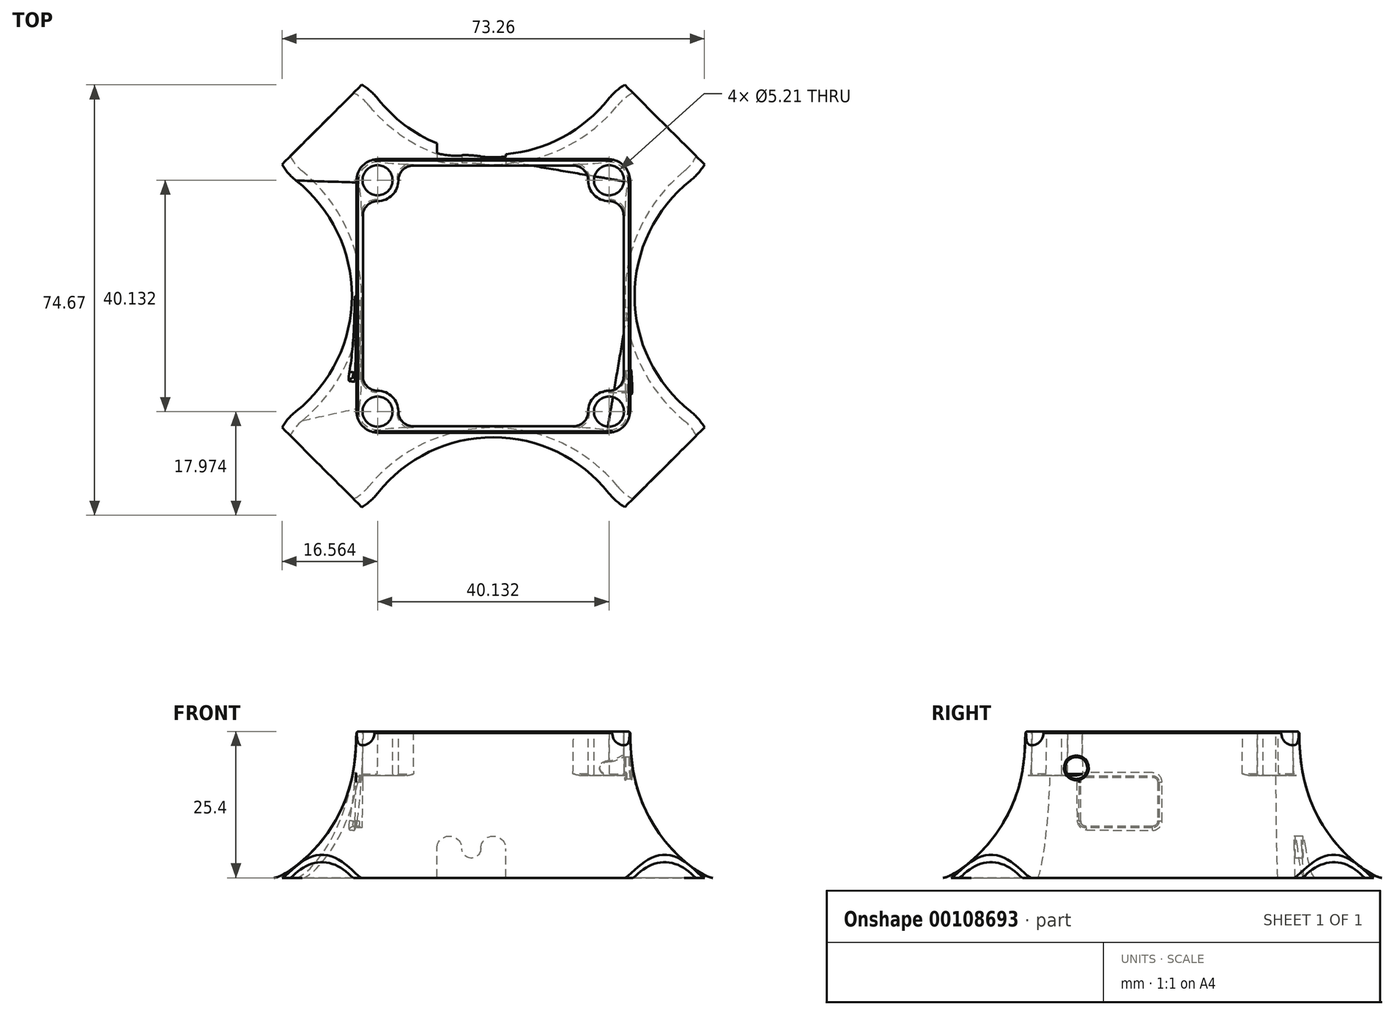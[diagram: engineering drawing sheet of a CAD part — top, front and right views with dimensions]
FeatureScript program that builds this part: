
annotation { "Feature Type Name" : "Feature", "Feature Type Description" : "" }
export const myFeature = defineFeature(function(context is Context, id is Id, definition is map)
    precondition{}
    {
        {
            var Q0;
            Q0=qCreatedBy(makeId("Top.planeOp"),FACE);
            var sketch = newSketch(context, id + "F0", { "sketchPlane" : qUnion([Q0])});
            skPoint(sketch, "E0.middle", {"position": v(0, 0) * mm});
            skCircle(sketch, "E1", {"center": v(-50.04, 0) * mm, "radius": 25.53 * mm});
            skCircle(sketch, "E2", {"center": v(50.04, 0) * mm, "radius": 25.53 * mm});
            skCircle(sketch, "E3", {"center": v(0, 50.04) * mm, "radius": 25.53 * mm});
            skCircle(sketch, "E4", {"center": v(0, -50.04) * mm, "radius": 25.53 * mm});
            skArc(sketch, "E5", {"start": v(-20.02, 34.2) * mm, "mid": v(-35.08, 35.08) * mm, "end": v(-34.2, 20.02) * mm});
            skArc(sketch, "E6", {"start": v(34.2, 20.02) * mm, "mid": v(35.08, 35.08) * mm, "end": v(20.02, 34.2) * mm});
            skArc(sketch, "E7", {"start": v(20.02, -34.2) * mm, "mid": v(35.08, -35.08) * mm, "end": v(34.2, -20.02) * mm});
            skArc(sketch, "E8", {"start": v(-34.2, -20.02) * mm, "mid": v(-35.08, -35.08) * mm, "end": v(-20.02, -34.2) * mm});
            skSolve(sketch);
        }
        {
            var Q0;
            Q0=qCreatedBy(makeId("Top.planeOp"),FACE);
            cPlane(context, id + "F1", {"entities" : qUnion([Q0]), "cplaneType" : CPlaneType.OFFSET, "offset" : 25.4 * mm, "width" : 152.4 * mm, "height" : 152.4 * mm});
        }
        {
            var Q0;
            Q0=qCreatedBy(id+"F1.planeOp",FACE);
            var sketch = newSketch(context, id + "F2", { "sketchPlane" : qUnion([Q0])});
            skLineSegment(sketch, "E9.bottom", {"start": v(19.69, 23.75) * mm, "end": v(-19.69, 23.75) * mm});
            skLineSegment(sketch, "E9.top", {"start": v(19.69, -23.75) * mm, "end": v(-19.69, -23.75) * mm});
            skLineSegment(sketch, "E9.left", {"start": v(23.75, 19.69) * mm, "end": v(23.75, -19.68) * mm});
            skLineSegment(sketch, "E9.right", {"start": v(-23.75, 19.69) * mm, "end": v(-23.75, -19.68) * mm});
            skPoint(sketch, "E9.middle", {"position": v(0, 0) * mm});
            skPoint(sketch, "E10.visualSharp", {"position": v(-23.75, 23.75) * mm});
            skArc(sketch, "E10.filletArc", {"start": v(-19.69, 23.75) * mm, "mid": v(-22.56, 22.56) * mm, "end": v(-23.75, 19.69) * mm});
            skPoint(sketch, "E11.visualSharp", {"position": v(23.75, 23.75) * mm});
            skArc(sketch, "E11.filletArc", {"start": v(23.75, 19.69) * mm, "mid": v(22.56, 22.56) * mm, "end": v(19.69, 23.75) * mm});
            skPoint(sketch, "E12.visualSharp", {"position": v(23.75, -23.75) * mm});
            skArc(sketch, "E12.filletArc", {"start": v(19.69, -23.75) * mm, "mid": v(22.56, -22.56) * mm, "end": v(23.75, -19.68) * mm});
            skPoint(sketch, "E13.visualSharp", {"position": v(-23.75, -23.75) * mm});
            skArc(sketch, "E13.filletArc", {"start": v(-23.75, -19.68) * mm, "mid": v(-22.56, -22.56) * mm, "end": v(-19.69, -23.75) * mm});
            skSolve(sketch);
        }
        {
            var Q0;
            {var subQ4=sQuery(id+"F0.wireOp",EDGE,"mulph02u-d4P1-MrBc-r413-ZnHLI4KnVT8I");var subQ12=sQuery(id+"F0.wireOp",EDGE,"E1");var subQ13=makeQuery(id+"F0.imprint","INTERSECT",VERTEX,{"disambiguationData":[OD(0.0)],"derivedFrom":[subQ12,subQ4]});Q0=makeQuery(id+"F0.imprint","IMPRINT",FACE,{"disambiguationData":[TD([[makeQuery(id+"F0.imprint","IMPRINT",EDGE,{"disambiguationData":[TD([[subQ13,-1.0]])],"derivedFrom":subQ12}),-1.0]])]});}
            var Q1;
            Q1=makeQuery(id+"F2.imprint","IMPRINT",FACE,{"disambiguationData":[TD([[makeQuery(id+"F2.imprint","IMPRINT",EDGE,{"derivedFrom":sQuery(id+"F2.wireOp",EDGE,"E9.bottom")}),1.0]])]});
            loft(context, id + "F3", {"startCondition" : LoftEndDerivativeType.TANGENT_TO_PROFILE, "startMagnitude" : .5, "endCondition" : LoftEndDerivativeType.NORMAL_TO_PROFILE, "endMagnitude" : 2, "sheetProfilesArray" : [{ "sheetProfileEntities" : qUnion([Q0]) }, { "sheetProfileEntities" : qUnion([Q1]) }]});
        }
        {
            var Q0;
            Q0=makeQuery(id+"F3.opLoft","CAP_FACE",FACE,{"disambiguationData":[OSD([makeQuery(id+"F2.imprint","IMPRINT",FACE,{"disambiguationData":[TD([[makeQuery(id+"F2.imprint","IMPRINT",EDGE,{"derivedFrom":sQuery(id+"F2.wireOp",EDGE,"E9.bottom")}),1.0]])]})])],"isStart":true});
            var sketch = newSketch(context, id + "F4", { "sketchPlane" : qUnion([Q0])});
            skLineSegment(sketch, "E14.bottom", {"start": v(19.3, 22.6) * mm, "end": v(-19.3, 22.6) * mm});
            skLineSegment(sketch, "E14.top", {"start": v(19.3, -22.6) * mm, "end": v(-19.3, -22.6) * mm});
            skLineSegment(sketch, "E14.left", {"start": v(22.6, 19.3) * mm, "end": v(22.6, -19.3) * mm});
            skLineSegment(sketch, "E14.right", {"start": v(-22.6, 19.3) * mm, "end": v(-22.6, -19.3) * mm});
            skPoint(sketch, "E14.middle", {"position": v(0, 0) * mm});
            skPoint(sketch, "E15.visualSharp", {"position": v(-22.6, 22.6) * mm});
            skArc(sketch, "E15.filletArc", {"start": v(-19.3, 22.6) * mm, "mid": v(-21.64, 21.64) * mm, "end": v(-22.6, 19.3) * mm});
            skPoint(sketch, "E16.visualSharp", {"position": v(22.6, 22.6) * mm});
            skArc(sketch, "E16.filletArc", {"start": v(22.6, 19.3) * mm, "mid": v(21.64, 21.64) * mm, "end": v(19.3, 22.6) * mm});
            skPoint(sketch, "E17.visualSharp", {"position": v(22.6, -22.6) * mm});
            skArc(sketch, "E17.filletArc", {"start": v(19.3, -22.6) * mm, "mid": v(21.64, -21.64) * mm, "end": v(22.6, -19.3) * mm});
            skPoint(sketch, "E18.visualSharp", {"position": v(-22.6, -22.6) * mm});
            skArc(sketch, "E18.filletArc", {"start": v(-22.6, -19.3) * mm, "mid": v(-21.64, -21.64) * mm, "end": v(-19.3, -22.6) * mm});
            skSolve(sketch);
        }
        {
            var Q0;
            Q0=qCreatedBy(makeId("Top.planeOp"),FACE);
            var sketch = newSketch(context, id + "F5", { "sketchPlane" : qUnion([Q0])});
            skCircle(sketch, "E19", {"center": v(-50.8, 0) * mm, "radius": 27.94 * mm});
            skCircle(sketch, "E20", {"center": v(0, -50.8) * mm, "radius": 27.94 * mm});
            skCircle(sketch, "E21", {"center": v(50.8, 0) * mm, "radius": 27.94 * mm});
            skCircle(sketch, "E22", {"center": v(0, 50.8) * mm, "radius": 27.94 * mm});
            skArc(sketch, "E23", {"start": v(-33.1, -21.62) * mm, "mid": v(-33.71, -33.71) * mm, "end": v(-21.62, -33.1) * mm});
            skArc(sketch, "E24", {"start": v(-21.62, 33.1) * mm, "mid": v(-33.71, 33.71) * mm, "end": v(-33.1, 21.62) * mm});
            skArc(sketch, "E25", {"start": v(33.1, 21.62) * mm, "mid": v(33.71, 33.71) * mm, "end": v(21.62, 33.1) * mm});
            skArc(sketch, "E26", {"start": v(21.62, -33.1) * mm, "mid": v(33.71, -33.71) * mm, "end": v(33.1, -21.62) * mm});
            skSolve(sketch);
        }
        {
            var Q1;
            {var subQ5=sQuery(id+"F5.wireOp",EDGE,"E23");Q1=makeQuery(id+"F5.imprint","IMPRINT",FACE,{"disambiguationData":[TD([[makeQuery(id+"F5.imprint","IMPRINT",EDGE,{"derivedFrom":subQ5}),1.0]])]});}
            var Q2;
            Q2=makeQuery(id+"F4.imprint","IMPRINT",FACE,{"disambiguationData":[TD([[makeQuery(id+"F4.imprint","IMPRINT",EDGE,{"derivedFrom":sQuery(id+"F4.wireOp",EDGE,"E14.bottom")}),1.0]])]});
            loft(context, id + "F6", {"operationType" : NewBodyOperationType.REMOVE, "startCondition" : LoftEndDerivativeType.TANGENT_TO_PROFILE, "startMagnitude" : .5, "endCondition" : LoftEndDerivativeType.NORMAL_TO_PROFILE, "endMagnitude" : 2, "sheetProfilesArray" : [{ "sheetProfileEntities" : qUnion([Q1]) }, { "sheetProfileEntities" : qUnion([Q2]) }]});
        }
        {
            var Q0;
            Q0=qCreatedBy(makeId("Front.planeOp"),FACE);
            var sketch = newSketch(context, id + "F7", { "sketchPlane" : qUnion([Q0])});
            skCircle(sketch, "E27", {"center": v(-7.62, 5.08) * mm, "radius": 2.16 * mm});
            skCircle(sketch, "E28", {"center": v(0, 5.08) * mm, "radius": 2.16 * mm});
            skLineSegment(sketch, "E29.bottom", {"start": v(2.16, 5.08) * mm, "end": v(-2.16, 5.08) * mm});
            skLineSegment(sketch, "E29.top", {"start": v(2.16, 0) * mm, "end": v(-2.16, 0) * mm});
            skLineSegment(sketch, "E29.left", {"start": v(2.16, 5.08) * mm, "end": v(2.16, 0) * mm});
            skLineSegment(sketch, "E29.right", {"start": v(-2.16, 5.08) * mm, "end": v(-2.16, 0) * mm});
            skLineSegment(sketch, "E30.bottom", {"start": v(-5.46, 5.08) * mm, "end": v(-9.78, 5.08) * mm});
            skLineSegment(sketch, "E30.top", {"start": v(-5.46, 0) * mm, "end": v(-9.78, 0) * mm});
            skLineSegment(sketch, "E30.left", {"start": v(-5.46, 5.08) * mm, "end": v(-5.46, 0) * mm});
            skLineSegment(sketch, "E30.right", {"start": v(-9.78, 5.08) * mm, "end": v(-9.78, 0) * mm});
            skArc(sketch, "E31", {"start": v(-5.46, 5.08) * mm, "mid": v(-3.81, 3.43) * mm, "end": v(-2.16, 5.08) * mm});
            skLineSegment(sketch, "E32", {"start": v(-5.46, 0) * mm, "end": v(-2.16, 0) * mm});
            skSolve(sketch);
        }
        {
            var Q0;
            Q0 = qSketchRegion(id + "F7", true);
            extrude(context, id + "F8", {"entities" : qUnion([Q0]), "operationType" : NewBodyOperationType.REMOVE, "endBound" : BoundingType.THROUGH_ALL, "oppositeDirection" : true, "depth" : 25.4 * mm});
        }
        {
            var Q0;
            Q0=qCreatedBy(makeId("Right.planeOp"),FACE);
            var sketch = newSketch(context, id + "F9", { "sketchPlane" : qUnion([Q0])});
            skLineSegment(sketch, "E33.bottom", {"start": v(-14.16, 17.46) * mm, "end": v(-0.83, 17.46) * mm});
            skLineSegment(sketch, "E33.top", {"start": v(-14.16, 8.95) * mm, "end": v(-0.83, 8.95) * mm});
            skLineSegment(sketch, "E33.left", {"start": v(-14.16, 17.46) * mm, "end": v(-14.16, 8.95) * mm});
            skLineSegment(sketch, "E33.right", {"start": v(-0.83, 17.46) * mm, "end": v(-0.83, 8.95) * mm});
            skPoint(sketch, "E33.middle", {"position": v(-7.5, 13.2) * mm});
            skSolve(sketch);
        }
        {
            var Q0;
            Q0 = qSketchRegion(id + "F9", true);
            extrude(context, id + "F10", {"entities" : qUnion([Q0]), "operationType" : NewBodyOperationType.REMOVE, "oppositeDirection" : true, "depth" : 27.94 * mm});
        }
        {
            var Q0;
            Q0=qCreatedBy(id+"F1.planeOp",FACE);
            var sketch = newSketch(context, id + "F11", { "sketchPlane" : qUnion([Q0])});
            skCircle(sketch, "E34", {"center": v(-20.07, 20.07) * mm, "radius": 2.6 * mm});
            skCircle(sketch, "E35", {"center": v(20.07, 20.07) * mm, "radius": 2.6 * mm});
            skCircle(sketch, "E36", {"center": v(20.07, -20.07) * mm, "radius": 2.6 * mm});
            skCircle(sketch, "E37", {"center": v(-20.07, -20.07) * mm, "radius": 2.6 * mm});
            skCircle(sketch, "E38", {"center": v(-20.07, 20.07) * mm, "radius": 3.62 * mm});
            skCircle(sketch, "E39", {"center": v(20.07, 20.07) * mm, "radius": 3.62 * mm});
            skCircle(sketch, "E40", {"center": v(20.07, -20.07) * mm, "radius": 3.62 * mm});
            skCircle(sketch, "E41", {"center": v(-20.07, -20.07) * mm, "radius": 3.62 * mm});
            skSolve(sketch);
        }
        {
            var Q0;
            Q0 = qSketchRegion(id + "F11", true);
            extrude(context, id + "F12", {"entities" : qUnion([Q0]), "operationType" : NewBodyOperationType.ADD, "oppositeDirection" : true, "depth" : 7.62 * mm});
        }
        {
            var Q0;
            Q0=makeQuery(id+"F11.imprint","IMPRINT",FACE,{"disambiguationData":[TD([[makeQuery(id+"F11.imprint","IMPRINT",EDGE,{"derivedFrom":sQuery(id+"F11.wireOp",EDGE,"E34")}),1.0]])]});
            var Q1;
            Q1=makeQuery(id+"F11.imprint","IMPRINT",FACE,{"disambiguationData":[TD([[makeQuery(id+"F11.imprint","IMPRINT",EDGE,{"derivedFrom":sQuery(id+"F11.wireOp",EDGE,"E35")}),1.0]])]});
            var Q2;
            Q2=makeQuery(id+"F11.imprint","IMPRINT",FACE,{"disambiguationData":[TD([[makeQuery(id+"F11.imprint","IMPRINT",EDGE,{"derivedFrom":sQuery(id+"F11.wireOp",EDGE,"E36")}),1.0]])]});
            var Q3;
            Q3=makeQuery(id+"F11.imprint","IMPRINT",FACE,{"disambiguationData":[TD([[makeQuery(id+"F11.imprint","IMPRINT",EDGE,{"derivedFrom":sQuery(id+"F11.wireOp",EDGE,"E37")}),1.0]])]});
            extrude(context, id + "F13", {"entities" : qUnion([Q0, Q1, Q2, Q3]), "operationType" : NewBodyOperationType.REMOVE, "oppositeDirection" : true, "depth" : 25.4 * mm});
        }
        {
            var Q0;
            Q0=qCreatedBy(makeId("Top.planeOp"),FACE);
            var sketch = newSketch(context, id + "F14", { "sketchPlane" : qUnion([Q0])});
            skLineSegment(sketch, "E42", {"start": v(-40.32, -19.12) * mm, "end": v(-21.86, -37.57) * mm});
            skLineSegment(sketch, "E43", {"start": v(-21.86, -37.57) * mm, "end": v(-34.9, -50.6) * mm});
            skLineSegment(sketch, "E44", {"start": v(-34.9, -50.6) * mm, "end": v(-53.35, -32.15) * mm});
            skLineSegment(sketch, "E45", {"start": v(-53.35, -32.15) * mm, "end": v(-40.32, -19.12) * mm});
            skLineSegment(sketch, "E46", {"start": v(18.93, -40.5) * mm, "end": v(41.3, -18.13) * mm});
            skLineSegment(sketch, "E47", {"start": v(41.3, -18.13) * mm, "end": v(54.22, -31.04) * mm});
            skLineSegment(sketch, "E48", {"start": v(54.22, -31.04) * mm, "end": v(31.85, -53.42) * mm});
            skLineSegment(sketch, "E49", {"start": v(31.85, -53.42) * mm, "end": v(18.93, -40.5) * mm});
            skLineSegment(sketch, "E50", {"start": v(19.12, 40.32) * mm, "end": v(39.94, 19.5) * mm});
            skLineSegment(sketch, "E51", {"start": v(39.94, 19.5) * mm, "end": v(51.75, 31.32) * mm});
            skLineSegment(sketch, "E52", {"start": v(51.75, 31.32) * mm, "end": v(30.93, 52.14) * mm});
            skLineSegment(sketch, "E53", {"start": v(30.93, 52.14) * mm, "end": v(19.12, 40.32) * mm});
            skLineSegment(sketch, "E54", {"start": v(-40.03, 19.4) * mm, "end": v(-18.43, 41.01) * mm});
            skLineSegment(sketch, "E55", {"start": v(-18.43, 41.01) * mm, "end": v(-28.85, 51.44) * mm});
            skLineSegment(sketch, "E56", {"start": v(-28.85, 51.44) * mm, "end": v(-50.46, 29.83) * mm});
            skLineSegment(sketch, "E57", {"start": v(-50.46, 29.83) * mm, "end": v(-40.03, 19.4) * mm});
            skSolve(sketch);
        }
        {
            var Q0;
            Q0 = qSketchRegion(id + "F14", true);
            extrude(context, id + "F15", {"entities" : qUnion([Q0]), "operationType" : NewBodyOperationType.REMOVE, "depth" : 7.62 * mm});
        }
        {
            var Q0;
            Q0=makeQuery(id+"F10.boolean.opBoolean","COPY",EDGE,{"derivedFrom":makeQuery(id+"F10.opExtrude","SWEPT_EDGE",EDGE,{"disambiguationData":[OSD([sQuery(id+"F9.wireOp",EDGE,"E33.bottom"),sQuery(id+"F9.wireOp",EDGE,"E33.right")])]})});
            var Q1;
            Q1=makeQuery(id+"F10.boolean.opBoolean","COPY",EDGE,{"derivedFrom":makeQuery(id+"F10.opExtrude","SWEPT_EDGE",EDGE,{"disambiguationData":[OSD([sQuery(id+"F9.wireOp",EDGE,"E33.bottom"),sQuery(id+"F9.wireOp",EDGE,"E33.left")])]})});
            var Q2;
            Q2=makeQuery(id+"F10.boolean.opBoolean","COPY",EDGE,{"derivedFrom":makeQuery(id+"F10.opExtrude","SWEPT_EDGE",EDGE,{"disambiguationData":[OSD([sQuery(id+"F9.wireOp",EDGE,"E33.top"),sQuery(id+"F9.wireOp",EDGE,"E33.right")])]})});
            var Q3;
            Q3=makeQuery(id+"F10.boolean.opBoolean","COPY",EDGE,{"derivedFrom":makeQuery(id+"F10.opExtrude","SWEPT_EDGE",EDGE,{"disambiguationData":[OSD([sQuery(id+"F9.wireOp",EDGE,"E33.top"),sQuery(id+"F9.wireOp",EDGE,"E33.left")])]})});
            fillet(context, id + "F16", {"entities" : qUnion([Q0, Q1, Q2, Q3]), "radius" : 0.89 * mm, "tangentPropagation" : true, "allowEdgeOverflow" : false});
        }
        {
            var Q0;
            Q0=makeQuery(id+"F10.boolean.opBoolean","INTERSECT",EDGE,{"derivedFrom":[makeQuery(id+"F6.boolean.opBoolean","COPY",FACE,{"derivedFrom":makeQuery(id+"F6.opLoft","SWEPT_FACE",FACE,{"disambiguationData":[OSD([sQuery(id+"F4.wireOp",EDGE,"E14.top"),sQuery(id+"F4.wireOp",EDGE,"E14.right"),sQuery(id+"F4.wireOp",EDGE,"E18.filletArc"),sQuery(id+"F5.wireOp",EDGE,"E19"),sQuery(id+"F5.wireOp",EDGE,"E20"),sQuery(id+"F5.wireOp",EDGE,"E23")])]})}),makeQuery(id+"F10.opExtrude","SWEPT_FACE",FACE,{"disambiguationData":[OSD([sQuery(id+"F9.wireOp",EDGE,"E33.bottom")])]})]});
            var Q1;
            Q1=makeQuery(id+"F10.boolean.opBoolean","INTERSECT",EDGE,{"derivedFrom":[makeQuery(id+"F6.boolean.opBoolean","COPY",FACE,{"derivedFrom":makeQuery(id+"F6.opLoft","SWEPT_FACE",FACE,{"disambiguationData":[OSD([sQuery(id+"F4.wireOp",EDGE,"E14.top"),sQuery(id+"F4.wireOp",EDGE,"E14.right"),sQuery(id+"F4.wireOp",EDGE,"E18.filletArc"),sQuery(id+"F5.wireOp",EDGE,"E19"),sQuery(id+"F5.wireOp",EDGE,"E20"),sQuery(id+"F5.wireOp",EDGE,"E23")])]})}),makeQuery(id+"F10.opExtrude","SWEPT_FACE",FACE,{"disambiguationData":[OSD([sQuery(id+"F9.wireOp",EDGE,"E33.left")])]})]});
            var Q2;
            Q2=makeQuery(id+"F10.boolean.opBoolean","INTERSECT",EDGE,{"derivedFrom":[makeQuery(id+"F6.boolean.opBoolean","COPY",FACE,{"derivedFrom":makeQuery(id+"F6.opLoft","SWEPT_FACE",FACE,{"disambiguationData":[OSD([sQuery(id+"F4.wireOp",EDGE,"E14.top"),sQuery(id+"F4.wireOp",EDGE,"E14.right"),sQuery(id+"F4.wireOp",EDGE,"E18.filletArc"),sQuery(id+"F5.wireOp",EDGE,"E19"),sQuery(id+"F5.wireOp",EDGE,"E20"),sQuery(id+"F5.wireOp",EDGE,"E23")])]})}),makeQuery(id+"F10.opExtrude","SWEPT_FACE",FACE,{"disambiguationData":[OSD([sQuery(id+"F9.wireOp",EDGE,"E33.top")])]})]});
            var Q3;
            Q3=makeQuery(id+"F10.boolean.opBoolean","INTERSECT",EDGE,{"derivedFrom":[makeQuery(id+"F6.boolean.opBoolean","COPY",FACE,{"derivedFrom":makeQuery(id+"F6.opLoft","SWEPT_FACE",FACE,{"disambiguationData":[OSD([sQuery(id+"F4.wireOp",EDGE,"E14.top"),sQuery(id+"F4.wireOp",EDGE,"E14.right"),sQuery(id+"F4.wireOp",EDGE,"E18.filletArc"),sQuery(id+"F5.wireOp",EDGE,"E19"),sQuery(id+"F5.wireOp",EDGE,"E20"),sQuery(id+"F5.wireOp",EDGE,"E23")])]})}),makeQuery(id+"F10.opExtrude","SWEPT_FACE",FACE,{"disambiguationData":[OSD([sQuery(id+"F9.wireOp",EDGE,"E33.right")])]})]});
            fillet(context, id + "F17", {"entities" : qUnion([Q0, Q1, Q2, Q3]), "radius" : 0.25 * mm, "tangentPropagation" : true, "allowEdgeOverflow" : false});
        }
        {
            var Q0;
            Q0=makeQuery(id+"F12.boolean.opBoolean","INTERSECT",EDGE,{"disambiguationData":[OD(2.0)],"derivedFrom":[makeQuery(id+"F6.boolean.opBoolean","COPY",FACE,{"derivedFrom":makeQuery(id+"F6.opLoft","SWEPT_FACE",FACE,{"disambiguationData":[OSD([sQuery(id+"F4.wireOp",EDGE,"E14.top"),sQuery(id+"F4.wireOp",EDGE,"E14.right"),sQuery(id+"F4.wireOp",EDGE,"E18.filletArc"),sQuery(id+"F5.wireOp",EDGE,"E19"),sQuery(id+"F5.wireOp",EDGE,"E20"),sQuery(id+"F5.wireOp",EDGE,"E23")])]})}),makeQuery(id+"F12.opExtrude","SWEPT_FACE",FACE,{"disambiguationData":[OSD([sQuery(id+"F11.wireOp",EDGE,"E41")])]})]});
            var Q1;
            Q1=makeQuery(id+"F12.boolean.opBoolean","INTERSECT",EDGE,{"disambiguationData":[OD(1.0)],"derivedFrom":[makeQuery(id+"F6.boolean.opBoolean","COPY",FACE,{"derivedFrom":makeQuery(id+"F6.opLoft","SWEPT_FACE",FACE,{"disambiguationData":[OSD([sQuery(id+"F4.wireOp",EDGE,"E14.top"),sQuery(id+"F4.wireOp",EDGE,"E14.right"),sQuery(id+"F4.wireOp",EDGE,"E18.filletArc"),sQuery(id+"F5.wireOp",EDGE,"E19"),sQuery(id+"F5.wireOp",EDGE,"E20"),sQuery(id+"F5.wireOp",EDGE,"E23")])]})}),makeQuery(id+"F12.opExtrude","SWEPT_FACE",FACE,{"disambiguationData":[OSD([sQuery(id+"F11.wireOp",EDGE,"E41")])]})]});
            var Q2;
            Q2=makeQuery(id+"F12.boolean.opBoolean","INTERSECT",EDGE,{"disambiguationData":[OD(2.0)],"derivedFrom":[makeQuery(id+"F6.boolean.opBoolean","COPY",FACE,{"derivedFrom":makeQuery(id+"F6.opLoft","SWEPT_FACE",FACE,{"disambiguationData":[OSD([sQuery(id+"F4.wireOp",EDGE,"E14.top"),sQuery(id+"F4.wireOp",EDGE,"E14.right"),sQuery(id+"F4.wireOp",EDGE,"E18.filletArc"),sQuery(id+"F5.wireOp",EDGE,"E19"),sQuery(id+"F5.wireOp",EDGE,"E20"),sQuery(id+"F5.wireOp",EDGE,"E23")])]})}),makeQuery(id+"F12.opExtrude","SWEPT_FACE",FACE,{"disambiguationData":[OSD([sQuery(id+"F11.wireOp",EDGE,"E38")])]})]});
            var Q3;
            Q3=makeQuery(id+"F12.boolean.opBoolean","INTERSECT",EDGE,{"disambiguationData":[OD(1.0)],"derivedFrom":[makeQuery(id+"F6.boolean.opBoolean","COPY",FACE,{"derivedFrom":makeQuery(id+"F6.opLoft","SWEPT_FACE",FACE,{"disambiguationData":[OSD([sQuery(id+"F4.wireOp",EDGE,"E14.top"),sQuery(id+"F4.wireOp",EDGE,"E14.right"),sQuery(id+"F4.wireOp",EDGE,"E18.filletArc"),sQuery(id+"F5.wireOp",EDGE,"E19"),sQuery(id+"F5.wireOp",EDGE,"E20"),sQuery(id+"F5.wireOp",EDGE,"E23")])]})}),makeQuery(id+"F12.opExtrude","SWEPT_FACE",FACE,{"disambiguationData":[OSD([sQuery(id+"F11.wireOp",EDGE,"E38")])]})]});
            var Q4;
            Q4=makeQuery(id+"F12.boolean.opBoolean","INTERSECT",EDGE,{"disambiguationData":[OD(2.0)],"derivedFrom":[makeQuery(id+"F6.boolean.opBoolean","COPY",FACE,{"derivedFrom":makeQuery(id+"F6.opLoft","SWEPT_FACE",FACE,{"disambiguationData":[OSD([sQuery(id+"F4.wireOp",EDGE,"E14.top"),sQuery(id+"F4.wireOp",EDGE,"E14.right"),sQuery(id+"F4.wireOp",EDGE,"E18.filletArc"),sQuery(id+"F5.wireOp",EDGE,"E19"),sQuery(id+"F5.wireOp",EDGE,"E20"),sQuery(id+"F5.wireOp",EDGE,"E23")])]})}),makeQuery(id+"F12.opExtrude","SWEPT_FACE",FACE,{"disambiguationData":[OSD([sQuery(id+"F11.wireOp",EDGE,"E39")])]})]});
            var Q5;
            Q5=makeQuery(id+"F12.boolean.opBoolean","INTERSECT",EDGE,{"disambiguationData":[OD(1.0)],"derivedFrom":[makeQuery(id+"F6.boolean.opBoolean","COPY",FACE,{"derivedFrom":makeQuery(id+"F6.opLoft","SWEPT_FACE",FACE,{"disambiguationData":[OSD([sQuery(id+"F4.wireOp",EDGE,"E14.top"),sQuery(id+"F4.wireOp",EDGE,"E14.right"),sQuery(id+"F4.wireOp",EDGE,"E18.filletArc"),sQuery(id+"F5.wireOp",EDGE,"E19"),sQuery(id+"F5.wireOp",EDGE,"E20"),sQuery(id+"F5.wireOp",EDGE,"E23")])]})}),makeQuery(id+"F12.opExtrude","SWEPT_FACE",FACE,{"disambiguationData":[OSD([sQuery(id+"F11.wireOp",EDGE,"E39")])]})]});
            var Q6;
            Q6=makeQuery(id+"F12.boolean.opBoolean","INTERSECT",EDGE,{"disambiguationData":[OD(1.0)],"derivedFrom":[makeQuery(id+"F6.boolean.opBoolean","COPY",FACE,{"derivedFrom":makeQuery(id+"F6.opLoft","SWEPT_FACE",FACE,{"disambiguationData":[OSD([sQuery(id+"F4.wireOp",EDGE,"E14.top"),sQuery(id+"F4.wireOp",EDGE,"E14.right"),sQuery(id+"F4.wireOp",EDGE,"E18.filletArc"),sQuery(id+"F5.wireOp",EDGE,"E19"),sQuery(id+"F5.wireOp",EDGE,"E20"),sQuery(id+"F5.wireOp",EDGE,"E23")])]})}),makeQuery(id+"F12.opExtrude","SWEPT_FACE",FACE,{"disambiguationData":[OSD([sQuery(id+"F11.wireOp",EDGE,"E40")])]})]});
            var Q7;
            Q7=makeQuery(id+"F12.boolean.opBoolean","INTERSECT",EDGE,{"disambiguationData":[OD(2.0)],"derivedFrom":[makeQuery(id+"F6.boolean.opBoolean","COPY",FACE,{"derivedFrom":makeQuery(id+"F6.opLoft","SWEPT_FACE",FACE,{"disambiguationData":[OSD([sQuery(id+"F4.wireOp",EDGE,"E14.top"),sQuery(id+"F4.wireOp",EDGE,"E14.right"),sQuery(id+"F4.wireOp",EDGE,"E18.filletArc"),sQuery(id+"F5.wireOp",EDGE,"E19"),sQuery(id+"F5.wireOp",EDGE,"E20"),sQuery(id+"F5.wireOp",EDGE,"E23")])]})}),makeQuery(id+"F12.opExtrude","SWEPT_FACE",FACE,{"disambiguationData":[OSD([sQuery(id+"F11.wireOp",EDGE,"E40")])]})]});
            fillet(context, id + "F18", {"entities" : qUnion([Q0, Q1, Q2, Q3, Q4, Q5, Q6, Q7]), "radius" : 2.54 * mm, "tangentPropagation" : true, "allowEdgeOverflow" : false});
        }
        {
            var Q0;
            {var subQ0=sQuery(id+"F11.wireOp",EDGE,"E35");Q0=makeQuery(id+"F13.boolean.opBoolean","MERGE",EDGE,{"derivedFrom":[makeQuery(id+"F12.opExtrude","CAP_EDGE",EDGE,{"disambiguationData":[OSD([subQ0])],"isStart":true}),makeQuery(id+"F13.opExtrude","CAP_EDGE",EDGE,{"disambiguationData":[OSD([subQ0])],"isStart":true})]});}
            var Q1;
            {var subQ0=sQuery(id+"F11.wireOp",EDGE,"E34");Q1=makeQuery(id+"F13.boolean.opBoolean","MERGE",EDGE,{"derivedFrom":[makeQuery(id+"F12.opExtrude","CAP_EDGE",EDGE,{"disambiguationData":[OSD([subQ0])],"isStart":true}),makeQuery(id+"F13.opExtrude","CAP_EDGE",EDGE,{"disambiguationData":[OSD([subQ0])],"isStart":true})]});}
            var Q2;
            {var subQ0=sQuery(id+"F11.wireOp",EDGE,"E36");Q2=makeQuery(id+"F13.boolean.opBoolean","MERGE",EDGE,{"derivedFrom":[makeQuery(id+"F12.opExtrude","CAP_EDGE",EDGE,{"disambiguationData":[OSD([subQ0])],"isStart":true}),makeQuery(id+"F13.opExtrude","CAP_EDGE",EDGE,{"disambiguationData":[OSD([subQ0])],"isStart":true})]});}
            var Q3;
            {var subQ0=sQuery(id+"F11.wireOp",EDGE,"E37");Q3=makeQuery(id+"F13.boolean.opBoolean","MERGE",EDGE,{"derivedFrom":[makeQuery(id+"F12.opExtrude","CAP_EDGE",EDGE,{"disambiguationData":[OSD([subQ0])],"isStart":true}),makeQuery(id+"F13.opExtrude","CAP_EDGE",EDGE,{"disambiguationData":[OSD([subQ0])],"isStart":true})]});}
            var Q4;
            Q4=makeQuery(id+"F12.opExtrude","CAP_EDGE",EDGE,{"disambiguationData":[OSD([sQuery(id+"F11.wireOp",EDGE,"E35")])],"isStart":false});
            var Q5;
            Q5=makeQuery(id+"F12.opExtrude","CAP_EDGE",EDGE,{"disambiguationData":[OSD([sQuery(id+"F11.wireOp",EDGE,"E34")])],"isStart":false});
            var Q6;
            Q6=makeQuery(id+"F12.opExtrude","CAP_EDGE",EDGE,{"disambiguationData":[OSD([sQuery(id+"F11.wireOp",EDGE,"E37")])],"isStart":false});
            var Q7;
            Q7=makeQuery(id+"F12.opExtrude","CAP_EDGE",EDGE,{"disambiguationData":[OSD([sQuery(id+"F11.wireOp",EDGE,"E36")])],"isStart":false});
            var Q8;
            {var subQ0=sQuery(id+"F11.wireOp",EDGE,"E40");Q8=makeQuery(id+"FeLZyzeFWoreKK9_1.opFillet","BLEND_EDGE",EDGE,{"blendedFrom":[makeQuery(id+"F12.boolean.opBoolean","INTERSECT",EDGE,{"disambiguationData":[OD(1.0)],"derivedFrom":[makeQuery(id+"F6.boolean.opBoolean","COPY",FACE,{"derivedFrom":makeQuery(id+"F6.opLoft","SWEPT_FACE",FACE,{"disambiguationData":[OSD([sQuery(id+"F4.wireOp",EDGE,"E14.top"),sQuery(id+"F4.wireOp",EDGE,"E14.right"),sQuery(id+"F4.wireOp",EDGE,"E18.filletArc"),sQuery(id+"F5.wireOp",EDGE,"E19"),sQuery(id+"F5.wireOp",EDGE,"E20"),sQuery(id+"F5.wireOp",EDGE,"E23")])]})}),makeQuery(id+"F12.opExtrude","SWEPT_FACE",FACE,{"disambiguationData":[OSD([subQ0])]})]}),makeQuery(id+"F12.opExtrude","CAP_FACE",FACE,{"disambiguationData":[OSD([sQuery(id+"F11.wireOp",EDGE,"E36"),subQ0])],"isStart":false})],"blendedInto":[makeQuery(id+"F12.opExtrude","CAP_FACE",FACE,{"disambiguationData":[OSD([sQuery(id+"F11.wireOp",EDGE,"E36"),subQ0])],"isStart":false})]});}
            var Q9;
            {var subQ0=sQuery(id+"F11.wireOp",EDGE,"E41");Q9=makeQuery(id+"FeLZyzeFWoreKK9_1.opFillet","BLEND_EDGE",EDGE,{"blendedFrom":[makeQuery(id+"F12.boolean.opBoolean","INTERSECT",EDGE,{"disambiguationData":[OD(0.0)],"derivedFrom":[makeQuery(id+"F6.boolean.opBoolean","COPY",FACE,{"derivedFrom":makeQuery(id+"F6.opLoft","SWEPT_FACE",FACE,{"disambiguationData":[OSD([sQuery(id+"F4.wireOp",EDGE,"E14.top"),sQuery(id+"F4.wireOp",EDGE,"E14.right"),sQuery(id+"F4.wireOp",EDGE,"E18.filletArc"),sQuery(id+"F5.wireOp",EDGE,"E19"),sQuery(id+"F5.wireOp",EDGE,"E20"),sQuery(id+"F5.wireOp",EDGE,"E23")])]})}),makeQuery(id+"F12.opExtrude","SWEPT_FACE",FACE,{"disambiguationData":[OSD([subQ0])]})]}),makeQuery(id+"F12.opExtrude","CAP_FACE",FACE,{"disambiguationData":[OSD([sQuery(id+"F11.wireOp",EDGE,"E37"),subQ0])],"isStart":false})],"blendedInto":[makeQuery(id+"F12.opExtrude","CAP_FACE",FACE,{"disambiguationData":[OSD([sQuery(id+"F11.wireOp",EDGE,"E37"),subQ0])],"isStart":false})]});}
            var Q10;
            {var subQ0=sQuery(id+"F11.wireOp",EDGE,"E38");Q10=makeQuery(id+"FeLZyzeFWoreKK9_1.opFillet","BLEND_EDGE",EDGE,{"blendedFrom":[makeQuery(id+"F12.boolean.opBoolean","INTERSECT",EDGE,{"disambiguationData":[OD(1.0)],"derivedFrom":[makeQuery(id+"F6.boolean.opBoolean","COPY",FACE,{"derivedFrom":makeQuery(id+"F6.opLoft","SWEPT_FACE",FACE,{"disambiguationData":[OSD([sQuery(id+"F4.wireOp",EDGE,"E14.top"),sQuery(id+"F4.wireOp",EDGE,"E14.right"),sQuery(id+"F4.wireOp",EDGE,"E18.filletArc"),sQuery(id+"F5.wireOp",EDGE,"E19"),sQuery(id+"F5.wireOp",EDGE,"E20"),sQuery(id+"F5.wireOp",EDGE,"E23")])]})}),makeQuery(id+"F12.opExtrude","SWEPT_FACE",FACE,{"disambiguationData":[OSD([subQ0])]})]}),makeQuery(id+"F12.opExtrude","CAP_FACE",FACE,{"disambiguationData":[OSD([sQuery(id+"F11.wireOp",EDGE,"E34"),subQ0])],"isStart":false})],"blendedInto":[makeQuery(id+"F12.opExtrude","CAP_FACE",FACE,{"disambiguationData":[OSD([sQuery(id+"F11.wireOp",EDGE,"E34"),subQ0])],"isStart":false})]});}
            var Q11;
            {var subQ0=sQuery(id+"F11.wireOp",EDGE,"E39");Q11=makeQuery(id+"FeLZyzeFWoreKK9_1.opFillet","BLEND_EDGE",EDGE,{"blendedFrom":[makeQuery(id+"F12.boolean.opBoolean","INTERSECT",EDGE,{"disambiguationData":[OD(0.0)],"derivedFrom":[makeQuery(id+"F6.boolean.opBoolean","COPY",FACE,{"derivedFrom":makeQuery(id+"F6.opLoft","SWEPT_FACE",FACE,{"disambiguationData":[OSD([sQuery(id+"F4.wireOp",EDGE,"E14.top"),sQuery(id+"F4.wireOp",EDGE,"E14.right"),sQuery(id+"F4.wireOp",EDGE,"E18.filletArc"),sQuery(id+"F5.wireOp",EDGE,"E19"),sQuery(id+"F5.wireOp",EDGE,"E20"),sQuery(id+"F5.wireOp",EDGE,"E23")])]})}),makeQuery(id+"F12.opExtrude","SWEPT_FACE",FACE,{"disambiguationData":[OSD([subQ0])]})]}),makeQuery(id+"F12.opExtrude","CAP_FACE",FACE,{"disambiguationData":[OSD([sQuery(id+"F11.wireOp",EDGE,"E35"),subQ0])],"isStart":false})],"blendedInto":[makeQuery(id+"F12.opExtrude","CAP_FACE",FACE,{"disambiguationData":[OSD([sQuery(id+"F11.wireOp",EDGE,"E35"),subQ0])],"isStart":false})]});}
            var Q12;
            Q12=makeQuery(id+"F6.boolean.opBoolean","COPY",EDGE,{"derivedFrom":makeQuery(id+"F6.opLoft","MID_CAP_EDGE",EDGE,{"disambiguationData":[OSD([sQuery(id+"F4.wireOp",EDGE,"E14.left"),sQuery(id+"F4.wireOp",EDGE,"E16.filletArc"),sQuery(id+"F4.wireOp",EDGE,"E17.filletArc")])],"capPos":1.0})});
            fillet(context, id + "F19", {"entities" : qUnion([Q0, Q1, Q2, Q3, Q4, Q5, Q6, Q7, Q8, Q9, Q10, Q11, Q12]), "radius" : 0.25 * mm, "tangentPropagation" : true, "allowEdgeOverflow" : false});
        }
        {
            var Q0;
            {var subQ0=sQuery(id+"F11.wireOp",EDGE,"E41");Q0=makeQuery(id+"F18.opFillet","BLEND_EDGE",EDGE,{"blendedFrom":[makeQuery(id+"F12.boolean.opBoolean","INTERSECT",EDGE,{"disambiguationData":[OD(1.0)],"derivedFrom":[makeQuery(id+"F6.boolean.opBoolean","COPY",FACE,{"derivedFrom":makeQuery(id+"F6.opLoft","SWEPT_FACE",FACE,{"disambiguationData":[OSD([sQuery(id+"F4.wireOp",EDGE,"E14.top"),sQuery(id+"F4.wireOp",EDGE,"E14.right"),sQuery(id+"F4.wireOp",EDGE,"E18.filletArc"),sQuery(id+"F5.wireOp",EDGE,"E19"),sQuery(id+"F5.wireOp",EDGE,"E20"),sQuery(id+"F5.wireOp",EDGE,"E23")])]})}),makeQuery(id+"F12.opExtrude","SWEPT_FACE",FACE,{"disambiguationData":[OSD([subQ0])]})]}),makeQuery(id+"F12.opExtrude","CAP_FACE",FACE,{"disambiguationData":[OSD([sQuery(id+"F11.wireOp",EDGE,"E37"),subQ0])],"isStart":false})],"blendedInto":[makeQuery(id+"F12.opExtrude","CAP_FACE",FACE,{"disambiguationData":[OSD([sQuery(id+"F11.wireOp",EDGE,"E37"),subQ0])],"isStart":false})]});}
            var Q1;
            {var subQ0=sQuery(id+"F11.wireOp",EDGE,"E40");Q1=makeQuery(id+"F18.opFillet","BLEND_EDGE",EDGE,{"blendedFrom":[makeQuery(id+"F12.boolean.opBoolean","INTERSECT",EDGE,{"disambiguationData":[OD(1.0)],"derivedFrom":[makeQuery(id+"F6.boolean.opBoolean","COPY",FACE,{"derivedFrom":makeQuery(id+"F6.opLoft","SWEPT_FACE",FACE,{"disambiguationData":[OSD([sQuery(id+"F4.wireOp",EDGE,"E14.top"),sQuery(id+"F4.wireOp",EDGE,"E14.right"),sQuery(id+"F4.wireOp",EDGE,"E18.filletArc"),sQuery(id+"F5.wireOp",EDGE,"E19"),sQuery(id+"F5.wireOp",EDGE,"E20"),sQuery(id+"F5.wireOp",EDGE,"E23")])]})}),makeQuery(id+"F12.opExtrude","SWEPT_FACE",FACE,{"disambiguationData":[OSD([subQ0])]})]}),makeQuery(id+"F12.opExtrude","CAP_FACE",FACE,{"disambiguationData":[OSD([sQuery(id+"F11.wireOp",EDGE,"E36"),subQ0])],"isStart":false})],"blendedInto":[makeQuery(id+"F12.opExtrude","CAP_FACE",FACE,{"disambiguationData":[OSD([sQuery(id+"F11.wireOp",EDGE,"E36"),subQ0])],"isStart":false})]});}
            var Q2;
            {var subQ0=sQuery(id+"F11.wireOp",EDGE,"E38");Q2=makeQuery(id+"F18.opFillet","BLEND_EDGE",EDGE,{"blendedFrom":[makeQuery(id+"F12.boolean.opBoolean","INTERSECT",EDGE,{"disambiguationData":[OD(1.0)],"derivedFrom":[makeQuery(id+"F6.boolean.opBoolean","COPY",FACE,{"derivedFrom":makeQuery(id+"F6.opLoft","SWEPT_FACE",FACE,{"disambiguationData":[OSD([sQuery(id+"F4.wireOp",EDGE,"E14.top"),sQuery(id+"F4.wireOp",EDGE,"E14.right"),sQuery(id+"F4.wireOp",EDGE,"E18.filletArc"),sQuery(id+"F5.wireOp",EDGE,"E19"),sQuery(id+"F5.wireOp",EDGE,"E20"),sQuery(id+"F5.wireOp",EDGE,"E23")])]})}),makeQuery(id+"F12.opExtrude","SWEPT_FACE",FACE,{"disambiguationData":[OSD([subQ0])]})]}),makeQuery(id+"F12.opExtrude","CAP_FACE",FACE,{"disambiguationData":[OSD([sQuery(id+"F11.wireOp",EDGE,"E34"),subQ0])],"isStart":false})],"blendedInto":[makeQuery(id+"F12.opExtrude","CAP_FACE",FACE,{"disambiguationData":[OSD([sQuery(id+"F11.wireOp",EDGE,"E34"),subQ0])],"isStart":false})]});}
            var Q3;
            {var subQ0=sQuery(id+"F11.wireOp",EDGE,"E39");Q3=makeQuery(id+"F18.opFillet","BLEND_EDGE",EDGE,{"blendedFrom":[makeQuery(id+"F12.boolean.opBoolean","INTERSECT",EDGE,{"disambiguationData":[OD(1.0)],"derivedFrom":[makeQuery(id+"F6.boolean.opBoolean","COPY",FACE,{"derivedFrom":makeQuery(id+"F6.opLoft","SWEPT_FACE",FACE,{"disambiguationData":[OSD([sQuery(id+"F4.wireOp",EDGE,"E14.top"),sQuery(id+"F4.wireOp",EDGE,"E14.right"),sQuery(id+"F4.wireOp",EDGE,"E18.filletArc"),sQuery(id+"F5.wireOp",EDGE,"E19"),sQuery(id+"F5.wireOp",EDGE,"E20"),sQuery(id+"F5.wireOp",EDGE,"E23")])]})}),makeQuery(id+"F12.opExtrude","SWEPT_FACE",FACE,{"disambiguationData":[OSD([subQ0])]})]}),makeQuery(id+"F12.opExtrude","CAP_FACE",FACE,{"disambiguationData":[OSD([sQuery(id+"F11.wireOp",EDGE,"E35"),subQ0])],"isStart":false})],"blendedInto":[makeQuery(id+"F12.opExtrude","CAP_FACE",FACE,{"disambiguationData":[OSD([sQuery(id+"F11.wireOp",EDGE,"E35"),subQ0])],"isStart":false})]});}
            var Q4;
            Q4=makeQuery(id+"F3.opLoft","MID_CAP_EDGE",EDGE,{"disambiguationData":[OSD([sQuery(id+"F2.wireOp",EDGE,"E9.bottom"),sQuery(id+"F2.wireOp",EDGE,"E10.filletArc"),sQuery(id+"F2.wireOp",EDGE,"E11.filletArc")])],"capPos":1.0});
            var Q5;
            Q5=makeQuery(id+"F12.boolean.opBoolean","SPLIT",EDGE,{"disambiguationData":[OD(0.0)],"derivedFrom":makeQuery(id+"F3.opLoft","MID_CAP_EDGE",EDGE,{"disambiguationData":[OSD([sQuery(id+"F2.wireOp",EDGE,"E9.bottom"),sQuery(id+"F2.wireOp",EDGE,"E9.right"),sQuery(id+"F2.wireOp",EDGE,"E10.filletArc")])],"capPos":1.0})});
            var Q6;
            {var subQ0=sQuery(id+"F11.wireOp",EDGE,"E38");var subQ1=sQuery(id+"F2.wireOp",EDGE,"E9.right");var subQ2=sQuery(id+"F2.wireOp",EDGE,"E9.bottom");var subQ3=sQuery(id+"F2.wireOp",EDGE,"E10.filletArc");Q6=makeQuery(id+"F12.boolean.opBoolean","SPLIT",EDGE,{"disambiguationData":[TD([makeQuery(id+"F3.opLoft","SWEPT_FACE",FACE,{"disambiguationData":[OSD([sQuery(id+"F0.wireOp",EDGE,"E1"),sQuery(id+"F0.wireOp",EDGE,"E3"),sQuery(id+"F0.wireOp",EDGE,"E5"),subQ2,subQ1,subQ3])]})])],"derivedFrom":makeQuery(id+"F12.opExtrude","CAP_EDGE",EDGE,{"disambiguationData":[OSD([subQ0])],"isStart":true})});}
            var Q7;
            Q7=makeQuery(id+"F3.opLoft","MID_CAP_EDGE",EDGE,{"disambiguationData":[OSD([sQuery(id+"F2.wireOp",EDGE,"E9.right"),sQuery(id+"F2.wireOp",EDGE,"E10.filletArc"),sQuery(id+"F2.wireOp",EDGE,"E13.filletArc")])],"capPos":1.0});
            var Q8;
            Q8=makeQuery(id+"F12.boolean.opBoolean","SPLIT",EDGE,{"disambiguationData":[OD(1.0)],"derivedFrom":makeQuery(id+"F3.opLoft","MID_CAP_EDGE",EDGE,{"disambiguationData":[OSD([sQuery(id+"F2.wireOp",EDGE,"E9.bottom"),sQuery(id+"F2.wireOp",EDGE,"E9.right"),sQuery(id+"F2.wireOp",EDGE,"E10.filletArc")])],"capPos":1.0})});
            var Q9;
            {var subQ0=sQuery(id+"F2.wireOp",EDGE,"E9.right");var subQ1=sQuery(id+"F2.wireOp",EDGE,"E9.bottom");var subQ2=sQuery(id+"F2.wireOp",EDGE,"E10.filletArc");var subQ3=sQuery(id+"F11.wireOp",EDGE,"E41");Q9=makeQuery(id+"F12.boolean.opBoolean","SPLIT",EDGE,{"disambiguationData":[TD([makeQuery(id+"F3.opLoft","SWEPT_FACE",FACE,{"disambiguationData":[OSD([sQuery(id+"F0.wireOp",EDGE,"E1"),sQuery(id+"F0.wireOp",EDGE,"E3"),sQuery(id+"F0.wireOp",EDGE,"E5"),subQ1,subQ0,subQ2])]})])],"derivedFrom":makeQuery(id+"F12.opExtrude","CAP_EDGE",EDGE,{"disambiguationData":[OSD([subQ3])],"isStart":true})});}
            var Q10;
            Q10=makeQuery(id+"F12.boolean.opBoolean","SPLIT",EDGE,{"disambiguationData":[OD(1.0)],"derivedFrom":makeQuery(id+"F3.opLoft","MID_CAP_EDGE",EDGE,{"disambiguationData":[OSD([sQuery(id+"F2.wireOp",EDGE,"E9.top"),sQuery(id+"F2.wireOp",EDGE,"E9.right"),sQuery(id+"F2.wireOp",EDGE,"E13.filletArc")])],"capPos":1.0})});
            var Q11;
            Q11=makeQuery(id+"F12.boolean.opBoolean","SPLIT",EDGE,{"disambiguationData":[OD(0.0)],"derivedFrom":makeQuery(id+"F3.opLoft","MID_CAP_EDGE",EDGE,{"disambiguationData":[OSD([sQuery(id+"F2.wireOp",EDGE,"E9.top"),sQuery(id+"F2.wireOp",EDGE,"E9.right"),sQuery(id+"F2.wireOp",EDGE,"E13.filletArc")])],"capPos":1.0})});
            var Q12;
            Q12=makeQuery(id+"F3.opLoft","MID_CAP_EDGE",EDGE,{"disambiguationData":[OSD([sQuery(id+"F2.wireOp",EDGE,"E9.top"),sQuery(id+"F2.wireOp",EDGE,"E12.filletArc"),sQuery(id+"F2.wireOp",EDGE,"E13.filletArc")])],"capPos":1.0});
            var Q13;
            Q13=makeQuery(id+"F12.boolean.opBoolean","SPLIT",EDGE,{"disambiguationData":[OD(0.0)],"derivedFrom":makeQuery(id+"F3.opLoft","MID_CAP_EDGE",EDGE,{"disambiguationData":[OSD([sQuery(id+"F2.wireOp",EDGE,"E9.top"),sQuery(id+"F2.wireOp",EDGE,"E9.left"),sQuery(id+"F2.wireOp",EDGE,"E12.filletArc")])],"capPos":1.0})});
            var Q14;
            {var subQ0=sQuery(id+"F2.wireOp",EDGE,"E9.right");var subQ1=sQuery(id+"F2.wireOp",EDGE,"E9.bottom");var subQ2=sQuery(id+"F2.wireOp",EDGE,"E10.filletArc");var subQ3=sQuery(id+"F11.wireOp",EDGE,"E40");Q14=makeQuery(id+"F12.boolean.opBoolean","SPLIT",EDGE,{"disambiguationData":[TD([makeQuery(id+"F3.opLoft","SWEPT_FACE",FACE,{"disambiguationData":[OSD([sQuery(id+"F0.wireOp",EDGE,"E1"),sQuery(id+"F0.wireOp",EDGE,"E3"),sQuery(id+"F0.wireOp",EDGE,"E5"),subQ1,subQ0,subQ2])]})])],"derivedFrom":makeQuery(id+"F12.opExtrude","CAP_EDGE",EDGE,{"disambiguationData":[OSD([subQ3])],"isStart":true})});}
            var Q15;
            Q15=makeQuery(id+"F3.opLoft","MID_CAP_EDGE",EDGE,{"disambiguationData":[OSD([sQuery(id+"F2.wireOp",EDGE,"E9.left"),sQuery(id+"F2.wireOp",EDGE,"E11.filletArc"),sQuery(id+"F2.wireOp",EDGE,"E12.filletArc")])],"capPos":1.0});
            var Q16;
            {var subQ0=sQuery(id+"F2.wireOp",EDGE,"E9.right");var subQ1=sQuery(id+"F2.wireOp",EDGE,"E9.bottom");var subQ2=sQuery(id+"F2.wireOp",EDGE,"E10.filletArc");var subQ3=sQuery(id+"F11.wireOp",EDGE,"E40");Q16=makeQuery(id+"F12.boolean.opBoolean","SPLIT",EDGE,{"disambiguationData":[TD([makeQuery(id+"F3.opLoft","SWEPT_FACE",FACE,{"disambiguationData":[OSD([sQuery(id+"F0.wireOp",EDGE,"E1"),sQuery(id+"F0.wireOp",EDGE,"E3"),sQuery(id+"F0.wireOp",EDGE,"E5"),subQ1,subQ0,subQ2])]})])],"derivedFrom":makeQuery(id+"F12.opExtrude","CAP_EDGE",EDGE,{"disambiguationData":[OSD([subQ3])],"isStart":true})});}
            var Q17;
            Q17=makeQuery(id+"F12.boolean.opBoolean","SPLIT",EDGE,{"disambiguationData":[OD(1.0)],"derivedFrom":makeQuery(id+"F3.opLoft","MID_CAP_EDGE",EDGE,{"disambiguationData":[OSD([sQuery(id+"F2.wireOp",EDGE,"E9.top"),sQuery(id+"F2.wireOp",EDGE,"E9.left"),sQuery(id+"F2.wireOp",EDGE,"E12.filletArc")])],"capPos":1.0})});
            var Q18;
            {var subQ0=sQuery(id+"F11.wireOp",EDGE,"E39");var subQ1=sQuery(id+"F2.wireOp",EDGE,"E9.right");var subQ2=sQuery(id+"F2.wireOp",EDGE,"E9.bottom");var subQ3=sQuery(id+"F2.wireOp",EDGE,"E10.filletArc");Q18=makeQuery(id+"F12.boolean.opBoolean","SPLIT",EDGE,{"disambiguationData":[TD([makeQuery(id+"F3.opLoft","SWEPT_FACE",FACE,{"disambiguationData":[OSD([sQuery(id+"F0.wireOp",EDGE,"E1"),sQuery(id+"F0.wireOp",EDGE,"E3"),sQuery(id+"F0.wireOp",EDGE,"E5"),subQ2,subQ1,subQ3])]})])],"derivedFrom":makeQuery(id+"F12.opExtrude","CAP_EDGE",EDGE,{"disambiguationData":[OSD([subQ0])],"isStart":true})});}
            var Q19;
            Q19=makeQuery(id+"F12.boolean.opBoolean","SPLIT",EDGE,{"disambiguationData":[OD(1.0)],"derivedFrom":makeQuery(id+"F3.opLoft","MID_CAP_EDGE",EDGE,{"disambiguationData":[OSD([sQuery(id+"F2.wireOp",EDGE,"E9.bottom"),sQuery(id+"F2.wireOp",EDGE,"E9.left"),sQuery(id+"F2.wireOp",EDGE,"E11.filletArc")])],"capPos":1.0})});
            var Q20;
            Q20=makeQuery(id+"F12.boolean.opBoolean","SPLIT",EDGE,{"disambiguationData":[OD(0.0)],"derivedFrom":makeQuery(id+"F3.opLoft","MID_CAP_EDGE",EDGE,{"disambiguationData":[OSD([sQuery(id+"F2.wireOp",EDGE,"E9.bottom"),sQuery(id+"F2.wireOp",EDGE,"E9.left"),sQuery(id+"F2.wireOp",EDGE,"E11.filletArc")])],"capPos":1.0})});
            fillet(context, id + "F20", {"entities" : qUnion([Q0, Q1, Q2, Q3, Q4, Q5, Q6, Q7, Q8, Q9, Q10, Q11, Q12, Q13, Q14, Q15, Q16, Q17, Q18, Q19, Q20]), "radius" : 0.25 * mm, "tangentPropagation" : true, "allowEdgeOverflow" : false});
        }
        {
            var Q0;
            Q0=makeQuery(id+"F10.boolean.opBoolean","INTERSECT",EDGE,{"derivedFrom":[makeQuery(id+"F3.opLoft","SWEPT_FACE",FACE,{"disambiguationData":[OSD([sQuery(id+"F0.wireOp",EDGE,"E1"),sQuery(id+"F0.wireOp",EDGE,"E3"),sQuery(id+"F0.wireOp",EDGE,"E5"),sQuery(id+"F2.wireOp",EDGE,"E9.bottom"),sQuery(id+"F2.wireOp",EDGE,"E9.right"),sQuery(id+"F2.wireOp",EDGE,"E10.filletArc")])]}),makeQuery(id+"F10.opExtrude","SWEPT_FACE",FACE,{"disambiguationData":[OSD([sQuery(id+"F9.wireOp",EDGE,"E33.top")])]})]});
            var Q1;
            Q1=makeQuery(id+"F10.boolean.opBoolean","INTERSECT",EDGE,{"derivedFrom":[makeQuery(id+"F3.opLoft","SWEPT_FACE",FACE,{"disambiguationData":[OSD([sQuery(id+"F0.wireOp",EDGE,"E1"),sQuery(id+"F0.wireOp",EDGE,"E3"),sQuery(id+"F0.wireOp",EDGE,"E5"),sQuery(id+"F2.wireOp",EDGE,"E9.bottom"),sQuery(id+"F2.wireOp",EDGE,"E9.right"),sQuery(id+"F2.wireOp",EDGE,"E10.filletArc")])]}),makeQuery(id+"F10.opExtrude","SWEPT_FACE",FACE,{"disambiguationData":[OSD([sQuery(id+"F9.wireOp",EDGE,"E33.right")])]})]});
            fillet(context, id + "F21", {"entities" : qUnion([Q0, Q1]), "radius" : 0.76 * mm, "tangentPropagation" : true, "allowEdgeOverflow" : false});
        }
        {
            var Q0;
            Q0=qCreatedBy(makeId("Right.planeOp"),FACE);
            var sketch = newSketch(context, id + "F22", { "sketchPlane" : qUnion([Q0])});
            skCircle(sketch, "E58", {"center": v(-14.93, 19.05) * mm, "radius": 1.9 * mm});
            skSolve(sketch);
        }
        {
            var Q0;
            Q0 = qSketchRegion(id + "F22", true);
            extrude(context, id + "F23", {"entities" : qUnion([Q0]), "operationType" : NewBodyOperationType.REMOVE, "endBound" : BoundingType.THROUGH_ALL, "depth" : 25.4 * mm});
        }
        {
            var Q0;
            Q0=makeQuery(id+"F23.boolean.opBoolean","INTERSECT",EDGE,{"derivedFrom":[makeQuery(id+"F3.opLoft","SWEPT_FACE",FACE,{"disambiguationData":[OSD([sQuery(id+"F0.wireOp",EDGE,"E1"),sQuery(id+"F0.wireOp",EDGE,"E3"),sQuery(id+"F0.wireOp",EDGE,"E5"),sQuery(id+"F2.wireOp",EDGE,"E9.bottom"),sQuery(id+"F2.wireOp",EDGE,"E9.right"),sQuery(id+"F2.wireOp",EDGE,"E10.filletArc")])]}),makeQuery(id+"F23.opExtrude","SWEPT_FACE",FACE,{"disambiguationData":[OSD([sQuery(id+"F22.wireOp",EDGE,"E58")])]})]});
            var Q1;
            Q1=makeQuery(id+"F23.boolean.opBoolean","INTERSECT",EDGE,{"derivedFrom":[makeQuery(id+"F12.boolean.opBoolean","SPLIT",FACE,{"disambiguationData":[TD([makeQuery(id+"F8.boolean.opBoolean","COPY",FACE,{"derivedFrom":makeQuery(id+"F8.opExtrude","SWEPT_FACE",FACE,{"disambiguationData":[OSD([sQuery(id+"F7.wireOp",EDGE,"E27")])]})})])],"derivedFrom":makeQuery(id+"F6.boolean.opBoolean","COPY",FACE,{"derivedFrom":makeQuery(id+"F6.opLoft","SWEPT_FACE",FACE,{"disambiguationData":[OSD([sQuery(id+"F4.wireOp",EDGE,"E14.top"),sQuery(id+"F4.wireOp",EDGE,"E14.right"),sQuery(id+"F4.wireOp",EDGE,"E18.filletArc"),sQuery(id+"F5.wireOp",EDGE,"E19"),sQuery(id+"F5.wireOp",EDGE,"E20"),sQuery(id+"F5.wireOp",EDGE,"E23")])]})})}),makeQuery(id+"F23.opExtrude","SWEPT_FACE",FACE,{"disambiguationData":[OSD([sQuery(id+"F22.wireOp",EDGE,"E58")])]})]});
            fillet(context, id + "F24", {"entities" : qUnion([Q0, Q1]), "radius" : 0.25 * mm, "tangentPropagation" : true, "allowEdgeOverflow" : false});
        }
    });
